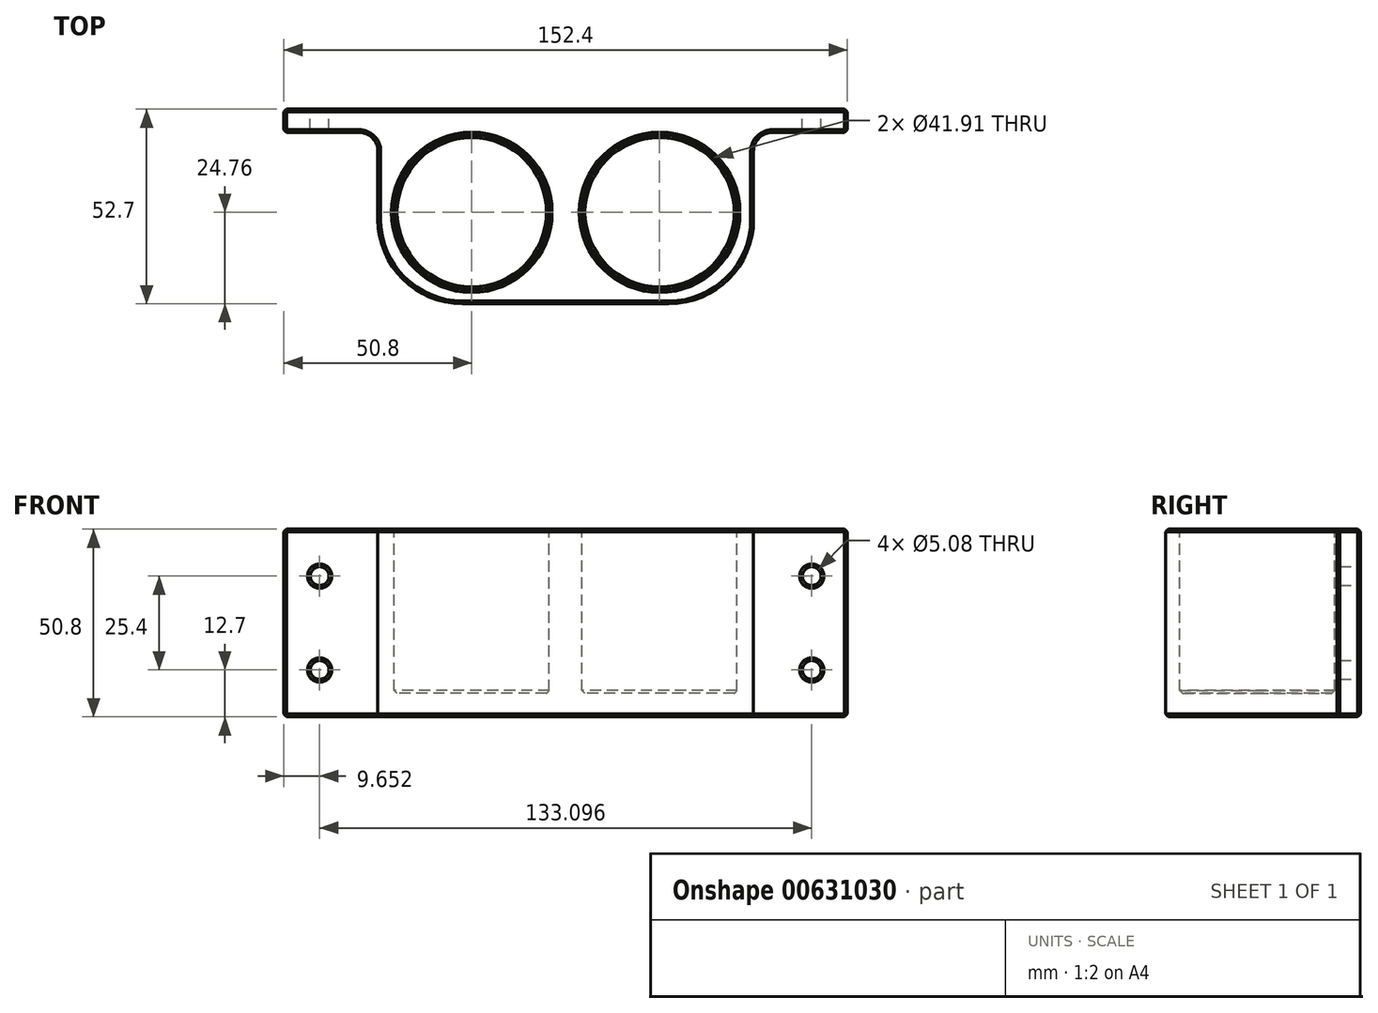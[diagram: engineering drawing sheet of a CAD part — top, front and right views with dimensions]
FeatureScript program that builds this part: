
annotation { "Feature Type Name" : "Feature", "Feature Type Description" : "" }
export const myFeature = defineFeature(function(context is Context, id is Id, definition is map)
    precondition{}
    {
        {
            var Q0;
            Q0=qCreatedBy(makeId("Front.planeOp"),FACE);
            var sketch = newSketch(context, id + "F0", { "sketchPlane" : qUnion([Q0])});
            skLineSegment(sketch, "E0.bottom", {"start": v(0, 0) * mm, "end": v(152.4, 0) * mm});
            skLineSegment(sketch, "E0.top", {"start": v(0, 50.8) * mm, "end": v(152.4, 50.8) * mm});
            skLineSegment(sketch, "E0.left", {"start": v(0, 0) * mm, "end": v(0, 50.8) * mm});
            skLineSegment(sketch, "E0.right", {"start": v(152.4, 0) * mm, "end": v(152.4, 50.8) * mm});
            skLineSegment(sketch, "E1", {"start": v(76.2, 50.8) * mm, "end": v(76.2, 0) * mm});
            skLineSegment(sketch, "E2.0", {"start": v(127, 50.8) * mm, "end": v(127, 0) * mm});
            skLineSegment(sketch, "E3.0", {"start": v(25.4, 50.8) * mm, "end": v(25.4, 0) * mm});
            skCircle(sketch, "E4", {"center": v(9.65, 38.1) * mm, "radius": 2.54 * mm});
            skCircle(sketch, "E5", {"center": v(9.65, 12.7) * mm, "radius": 2.54 * mm});
            skCircle(sketch, "E6", {"center": v(142.75, 12.7) * mm, "radius": 2.54 * mm});
            skCircle(sketch, "E7", {"center": v(142.75, 38.1) * mm, "radius": 2.54 * mm});
            skSolve(sketch);
        }
        {
            var Q0;
            {var subQ1=sQuery(id+"F0.wireOp",EDGE,"E0.left");Q0=makeQuery(id+"F0.imprint","IMPRINT",FACE,{"disambiguationData":[TD([[makeQuery(id+"F0.imprint","IMPRINT",EDGE,{"derivedFrom":subQ1}),-1.0]])]});}
            var Q1;
            {var subQ1=sQuery(id+"F0.wireOp",EDGE,"E0.right");Q1=makeQuery(id+"F0.imprint","IMPRINT",FACE,{"disambiguationData":[TD([[makeQuery(id+"F0.imprint","IMPRINT",EDGE,{"derivedFrom":subQ1}),1.0]])]});}
            var Q2;
            {var subQ0=sQuery(id+"F0.wireOp",EDGE,"E1");Q2=makeQuery(id+"F0.imprint","IMPRINT",FACE,{"disambiguationData":[TD([[makeQuery(id+"F0.imprint","IMPRINT",EDGE,{"derivedFrom":subQ0}),-1.0]])]});}
            var Q3;
            {var subQ0=sQuery(id+"F0.wireOp",EDGE,"E1");Q3=makeQuery(id+"F0.imprint","IMPRINT",FACE,{"disambiguationData":[TD([[makeQuery(id+"F0.imprint","IMPRINT",EDGE,{"derivedFrom":subQ0}),1.0]])]});}
            extrude(context, id + "F1", {"entities" : qUnion([Q0, Q1, Q2, Q3]), "depth" : 6.35 * mm, "offsetDistance" : 25.4 * mm});
        }
        {
            var Q0;
            {var subQ0=sQuery(id+"F0.wireOp",EDGE,"E1");Q0=makeQuery(id+"F0.imprint","IMPRINT",FACE,{"disambiguationData":[TD([[makeQuery(id+"F0.imprint","IMPRINT",EDGE,{"derivedFrom":subQ0}),-1.0]])]});}
            var Q1;
            {var subQ0=sQuery(id+"F0.wireOp",EDGE,"E1");Q1=makeQuery(id+"F0.imprint","IMPRINT",FACE,{"disambiguationData":[TD([[makeQuery(id+"F0.imprint","IMPRINT",EDGE,{"derivedFrom":subQ0}),1.0]])]});}
            extrude(context, id + "F2", {"entities" : qUnion([Q0, Q1]), "operationType" : NewBodyOperationType.ADD, "depth" : 52.7 * mm, "offsetDistance" : 25.4 * mm});
        }
        {
            var Q0;
            Q0=makeQuery(id+"F2.boolean.opBoolean","INTERSECT",EDGE,{"derivedFrom":[makeQuery(id+"F1.opExtrude","CAP_FACE",FACE,{"disambiguationData":[OSD([sQuery(id+"F0.wireOp",EDGE,"E0.bottom"),sQuery(id+"F0.wireOp",EDGE,"E0.top"),sQuery(id+"F0.wireOp",EDGE,"E0.left"),sQuery(id+"F0.wireOp",EDGE,"E0.right"),sQuery(id+"F0.wireOp",EDGE,"E4"),sQuery(id+"F0.wireOp",EDGE,"E5"),sQuery(id+"F0.wireOp",EDGE,"E6"),sQuery(id+"F0.wireOp",EDGE,"E7")])],"isStart":false}),makeQuery(id+"F2.opExtrude","SWEPT_FACE",FACE,{"disambiguationData":[OSD([sQuery(id+"F0.wireOp",EDGE,"E2.0")])]})]});
            var Q1;
            Q1=makeQuery(id+"F2.boolean.opBoolean","INTERSECT",EDGE,{"derivedFrom":[makeQuery(id+"F1.opExtrude","CAP_FACE",FACE,{"disambiguationData":[OSD([sQuery(id+"F0.wireOp",EDGE,"E0.bottom"),sQuery(id+"F0.wireOp",EDGE,"E0.top"),sQuery(id+"F0.wireOp",EDGE,"E0.left"),sQuery(id+"F0.wireOp",EDGE,"E0.right"),sQuery(id+"F0.wireOp",EDGE,"E4"),sQuery(id+"F0.wireOp",EDGE,"E5"),sQuery(id+"F0.wireOp",EDGE,"E6"),sQuery(id+"F0.wireOp",EDGE,"E7")])],"isStart":false}),makeQuery(id+"F2.opExtrude","SWEPT_FACE",FACE,{"disambiguationData":[OSD([sQuery(id+"F0.wireOp",EDGE,"E3.0")])]})]});
            fillet(context, id + "F3", {"entities" : qUnion([Q0, Q1]), "radius" : 5.08 * mm, "tangentPropagation" : true, "allowEdgeOverflow" : false});
        }
        {
            var Q0;
            {var subQ0=sQuery(id+"F0.wireOp",EDGE,"E0.top");Q0=makeQuery(id+"F2.boolean.opBoolean","MERGE",FACE,{"derivedFrom":[makeQuery(id+"F1.opExtrude","SWEPT_FACE",FACE,{"disambiguationData":[OSD([subQ0])]}),makeQuery(id+"F2.opExtrude","SWEPT_FACE",FACE,{"disambiguationData":[OSD([subQ0])]})]});}
            var sketch = newSketch(context, id + "F4", { "sketchPlane" : qUnion([Q0])});
            skPoint(sketch, "E8.centerSnap0", {"position": v(76.2, 0) * mm});
            skCircle(sketch, "E9", {"center": v(50.8, -27.94) * mm, "radius": 20.96 * mm});
            skCircle(sketch, "E10", {"center": v(101.6, -27.94) * mm, "radius": 20.96 * mm});
            skSolve(sketch);
        }
        {
            var Q0;
            Q0=makeQuery(id+"F4.imprint","IMPRINT",FACE,{"disambiguationData":[TD([[makeQuery(id+"F4.imprint","IMPRINT",EDGE,{"derivedFrom":sQuery(id+"F4.wireOp",EDGE,"E9")}),1.0]])]});
            var Q1;
            Q1=makeQuery(id+"F4.imprint","IMPRINT",FACE,{"disambiguationData":[TD([[makeQuery(id+"F4.imprint","IMPRINT",EDGE,{"derivedFrom":sQuery(id+"F4.wireOp",EDGE,"E10")}),1.0]])]});
            extrude(context, id + "F5", {"entities" : qUnion([Q0, Q1]), "operationType" : NewBodyOperationType.REMOVE, "oppositeDirection" : true, "depth" : 44.45 * mm, "offsetDistance" : 25.4 * mm});
        }
        {
            var Q0;
            Q0=makeQuery(id+"F2.opExtrude","CAP_EDGE",EDGE,{"disambiguationData":[OSD([sQuery(id+"F0.wireOp",EDGE,"E2.0")])],"isStart":false});
            var Q1;
            Q1=makeQuery(id+"F2.opExtrude","CAP_EDGE",EDGE,{"disambiguationData":[OSD([sQuery(id+"F0.wireOp",EDGE,"E3.0")])],"isStart":false});
            fillet(context, id + "F6", {"entities" : qUnion([Q0, Q1]), "radius" : 22.86 * mm, "tangentPropagation" : true, "allowEdgeOverflow" : false});
        }
        {
            var Q0;
            {var subQ0=sQuery(id+"F0.wireOp",EDGE,"E0.top");Q0=makeQuery(id+"F2.boolean.opBoolean","MERGE",FACE,{"derivedFrom":[makeQuery(id+"F1.opExtrude","SWEPT_FACE",FACE,{"disambiguationData":[OSD([subQ0])]}),makeQuery(id+"F2.opExtrude","SWEPT_FACE",FACE,{"disambiguationData":[OSD([subQ0])]})]});}
            var Q1;
            {var subQ0=sQuery(id+"F0.wireOp",EDGE,"E4");var subQ1=sQuery(id+"F0.wireOp",EDGE,"E0.left");var subQ2=sQuery(id+"F0.wireOp",EDGE,"E0.bottom");var subQ3=sQuery(id+"F0.wireOp",EDGE,"E0.top");var subQ4=sQuery(id+"F0.wireOp",EDGE,"E5");Q1=makeQuery(id+"F2.boolean.opBoolean","SPLIT",FACE,{"disambiguationData":[TD([makeQuery(id+"F1.opExtrude","SWEPT_FACE",FACE,{"disambiguationData":[OSD([subQ1])]})])],"derivedFrom":makeQuery(id+"F1.opExtrude","CAP_FACE",FACE,{"disambiguationData":[OSD([subQ2,subQ3,subQ1,sQuery(id+"F0.wireOp",EDGE,"E0.right"),subQ0,subQ4,sQuery(id+"F0.wireOp",EDGE,"E6"),sQuery(id+"F0.wireOp",EDGE,"E7")])],"isStart":false})});}
            var Q2;
            {var subQ0=sQuery(id+"F0.wireOp",EDGE,"E6");var subQ1=sQuery(id+"F0.wireOp",EDGE,"E0.top");var subQ2=sQuery(id+"F0.wireOp",EDGE,"E0.right");var subQ3=sQuery(id+"F0.wireOp",EDGE,"E0.bottom");var subQ4=sQuery(id+"F0.wireOp",EDGE,"E7");Q2=makeQuery(id+"F2.boolean.opBoolean","SPLIT",FACE,{"disambiguationData":[TD([makeQuery(id+"F1.opExtrude","SWEPT_FACE",FACE,{"disambiguationData":[OSD([subQ2])]})])],"derivedFrom":makeQuery(id+"F1.opExtrude","CAP_FACE",FACE,{"disambiguationData":[OSD([subQ3,subQ1,sQuery(id+"F0.wireOp",EDGE,"E0.left"),subQ2,sQuery(id+"F0.wireOp",EDGE,"E4"),sQuery(id+"F0.wireOp",EDGE,"E5"),subQ0,subQ4])],"isStart":false})});}
            var Q3;
            {var subQ0=sQuery(id+"F0.wireOp",EDGE,"E0.bottom");Q3=makeQuery(id+"F2.boolean.opBoolean","MERGE",FACE,{"derivedFrom":[makeQuery(id+"F1.opExtrude","SWEPT_FACE",FACE,{"disambiguationData":[OSD([subQ0])]}),makeQuery(id+"F2.opExtrude","SWEPT_FACE",FACE,{"disambiguationData":[OSD([subQ0])]})]});}
            var Q4;
            Q4=makeQuery(id+"F1.opExtrude","CAP_FACE",FACE,{"disambiguationData":[OSD([sQuery(id+"F0.wireOp",EDGE,"E0.bottom"),sQuery(id+"F0.wireOp",EDGE,"E0.top"),sQuery(id+"F0.wireOp",EDGE,"E0.left"),sQuery(id+"F0.wireOp",EDGE,"E0.right"),sQuery(id+"F0.wireOp",EDGE,"E4"),sQuery(id+"F0.wireOp",EDGE,"E5"),sQuery(id+"F0.wireOp",EDGE,"E6"),sQuery(id+"F0.wireOp",EDGE,"E7")])],"isStart":true});
            var Q5;
            Q5=makeQuery(id+"F5.boolean.opBoolean","COPY",EDGE,{"derivedFrom":makeQuery(id+"F5.opExtrude","CAP_EDGE",EDGE,{"disambiguationData":[OSD([sQuery(id+"F4.wireOp",EDGE,"E9")])],"isStart":false})});
            var Q6;
            Q6=makeQuery(id+"F5.boolean.opBoolean","COPY",EDGE,{"derivedFrom":makeQuery(id+"F5.opExtrude","CAP_EDGE",EDGE,{"disambiguationData":[OSD([sQuery(id+"F4.wireOp",EDGE,"E10")])],"isStart":false})});
            chamfer(context, id + "F7", {"entities" : qUnion([Q0, Q1, Q2, Q3, Q4, Q5, Q6]), "width" : 0.76 * mm, "tangentPropagation" : true});
        }
    });
